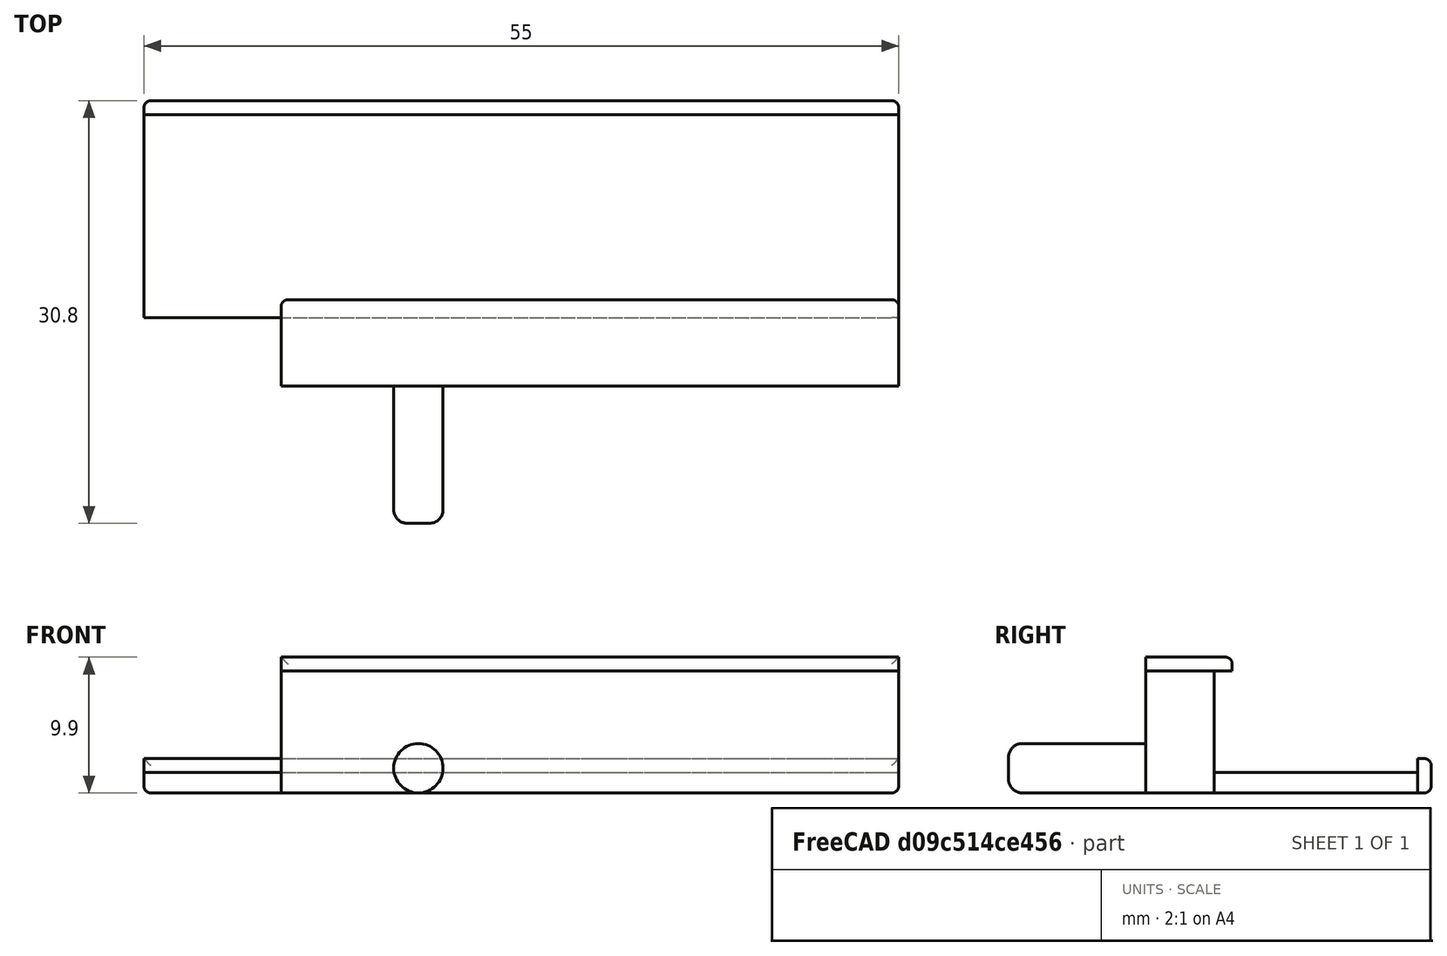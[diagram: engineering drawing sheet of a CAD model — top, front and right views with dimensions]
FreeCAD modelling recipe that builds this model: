
FCSTD DOCUMENT  (FreeCAD 0.21R33771 (Git))
Label: usb-support-2-round
License: All rights reserved
LicenseURL: http://en.wikipedia.org/wiki/All_rights_reserved
objects: Part::Fillet×5, Part::Box×4, Part::Cylinder×1
note: 10 computed .brp shape members not serialized (recipe doc carries the construction recipe); baked Part::Feature solids carry a one-line shape summary decoded from their .brp

FEATURE [Part::Box] Box  label="Cube"
  AttacherType = Attacher::AttachEngine3D
  Height = 8.9
  Length = 45
  Placement = pos=(10,0,0) rot=(0,0,1;0rad)
  Width = 5
FEATURE [Part::Box] Box001  label="Cube001"
  AttacherType = Attacher::AttachEngine3D
  Height = 1.5
  Length = 55
  Placement = pos=(0,5,0) rot=(0,0,1;0rad)
  Width = 14.8
FEATURE [Part::Box] Box002  label="Cube002"
  AttacherType = Attacher::AttachEngine3D
  Height = 2.5
  Length = 55
  Placement = pos=(0,19.8,0) rot=(0,0,1;0rad)
  Width = 1
FEATURE [Part::Box] Box003  label="Cube003"
  AttacherType = Attacher::AttachEngine3D
  Height = 1
  Length = 45
  Placement = pos=(10,0,8.9) rot=(0,0,1;0rad)
  Width = 6.3
FEATURE [Part::Cylinder] Cylinder
  Angle = 360
  AttacherType = Attacher::AttachEngine3D
  FirstAngle = 0
  Height = 10
  Placement = pos=(20,0,1.8) rot=(1,0,0;1.5708rad)
  Radius = 1.8
  SecondAngle = 0
FEATURE [Part::Fillet] Fillet
  Base = -> Cylinder
  Edges = 1 edges r=1: [Edge3]
FEATURE [Part::Fillet] Fillet001
  Base = -> Box002
  Edges = 6 edges r=0.5: [Edge3,Edge4,Edge7,Edge8,Edge11,Edge12]
FEATURE [Part::Fillet] Fillet003
  Base = -> Box001
  Edges = 2 edges r=0.5: [Edge4,Edge8]
FEATURE [Part::Fillet] Fillet004
  Base = -> Box
  Edges = 1 edges r=0.5: [Edge8]
FEATURE [Part::Fillet] Fillet005
  Base = -> Box003
  Edges = 3 edges r=0.5: [Edge3,Edge7,Edge12]
